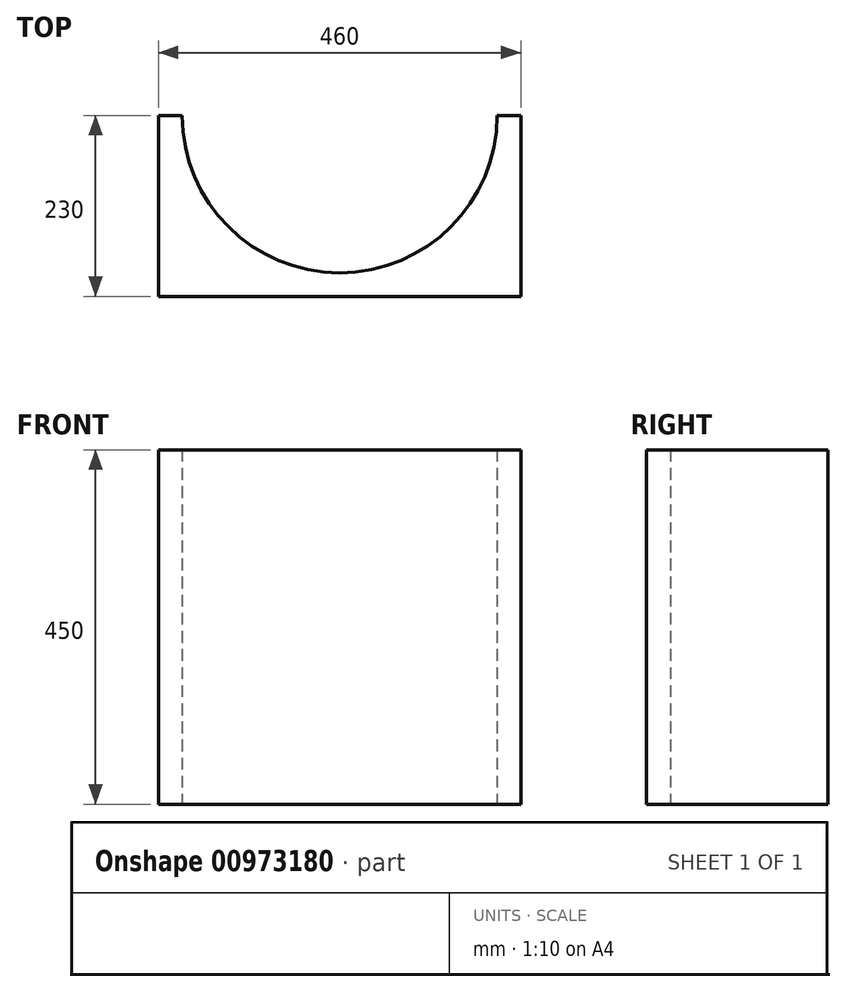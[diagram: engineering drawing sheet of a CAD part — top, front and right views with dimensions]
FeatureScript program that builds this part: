
annotation { "Feature Type Name" : "Feature", "Feature Type Description" : "" }
export const myFeature = defineFeature(function(context is Context, id is Id, definition is map)
    precondition{}
    {
        {
            var Q0;
            Q0=qCreatedBy(makeId("Top.planeOp"),FACE);
            var sketch = newSketch(context, id + "F0", { "sketchPlane" : qUnion([Q0])});
            skCircle(sketch, "E0", {"center": v(0, 0) * mm, "radius": 200 * mm});
            skSolve(sketch);
        }
        {
            var Q0;
            Q0 = qSketchRegion(id + "F0", true);
            extrude(context, id + "F1", {"entities" : qUnion([Q0]), "endBound" : BoundingType.SYMMETRIC, "depth" : 450 * mm, "offsetDistance" : 25 * mm});
        }
        {
            var Q0;
            Q0=qCreatedBy(makeId("Front.planeOp"),FACE);
            var sketch = newSketch(context, id + "F2", { "sketchPlane" : qUnion([Q0])});
            skLineSegment(sketch, "E1.bottom", {"start": v(230, -225) * mm, "end": v(-230, -225) * mm});
            skLineSegment(sketch, "E1.top", {"start": v(230, 225) * mm, "end": v(-230, 225) * mm});
            skLineSegment(sketch, "E1.left", {"start": v(230, -225) * mm, "end": v(230, 225) * mm});
            skLineSegment(sketch, "E1.right", {"start": v(-230, -225) * mm, "end": v(-230, 225) * mm});
            skPoint(sketch, "E1.middle", {"position": v(0, 0) * mm});
            skSolve(sketch);
        }
        {
            var Q0;
            Q0=makeQuery(id+"F2.imprint","IMPRINT",FACE,{"disambiguationData":[TD([[makeQuery(id+"F2.imprint","IMPRINT",EDGE,{"derivedFrom":sQuery(id+"F2.wireOp",EDGE,"E1.bottom")}),-1.0]])]});
            extrude(context, id + "F3", {"entities" : qUnion([Q0]), "depth" : 230 * mm, "offsetDistance" : 25 * mm});
        }
        {
            var Q0;
            Q0=makeQuery(id+"F1.opExtrude","SWEPT_BODY",BODY,{"disambiguationData":[OSD([sQuery(id+"F0.wireOp",EDGE,"E0")])]});
            var Q1;
            Q1=makeQuery(id+"F3.opExtrude","SWEPT_BODY",BODY,{"disambiguationData":[OSD([sQuery(id+"F2.wireOp",EDGE,"E1.bottom"),sQuery(id+"F2.wireOp",EDGE,"E1.top"),sQuery(id+"F2.wireOp",EDGE,"E1.left"),sQuery(id+"F2.wireOp",EDGE,"E1.right")])]});
            booleanBodies(context, id + "F4", {"operationType" : BooleanOperationType.SUBTRACTION, "tools" : qUnion([Q0]), "targets" : qUnion([Q1])});
        }
    });
